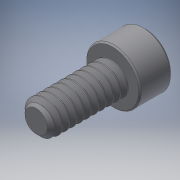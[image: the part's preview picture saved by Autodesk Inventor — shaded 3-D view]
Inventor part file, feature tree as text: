
AUTODESK INVENTOR PART (.ipt)
format: ipt  version: 2019 (Build 230136000, 136)  size: 536,064 bytes
history: native  units: in
note: dims shown in document units (in); Inventor stores cm internally (conversion verified against a paired STEP export)
features: chamfer x1
ambient origin geometry x8: Origin, YZ Plane, XZ Plane, XY Plane, X Axis, Y Axis, Z Axis, Center Point
bodies: Solid1 (feature_tree)
feature tree (1):
  chamfer  "Chamfer2"  [1 undecoded]
note: 1 required parameter value undecoded (feature->parameter linkage not recoverable at this tier; creation-order binding heuristic only, values carry confidence <= 0.55)
